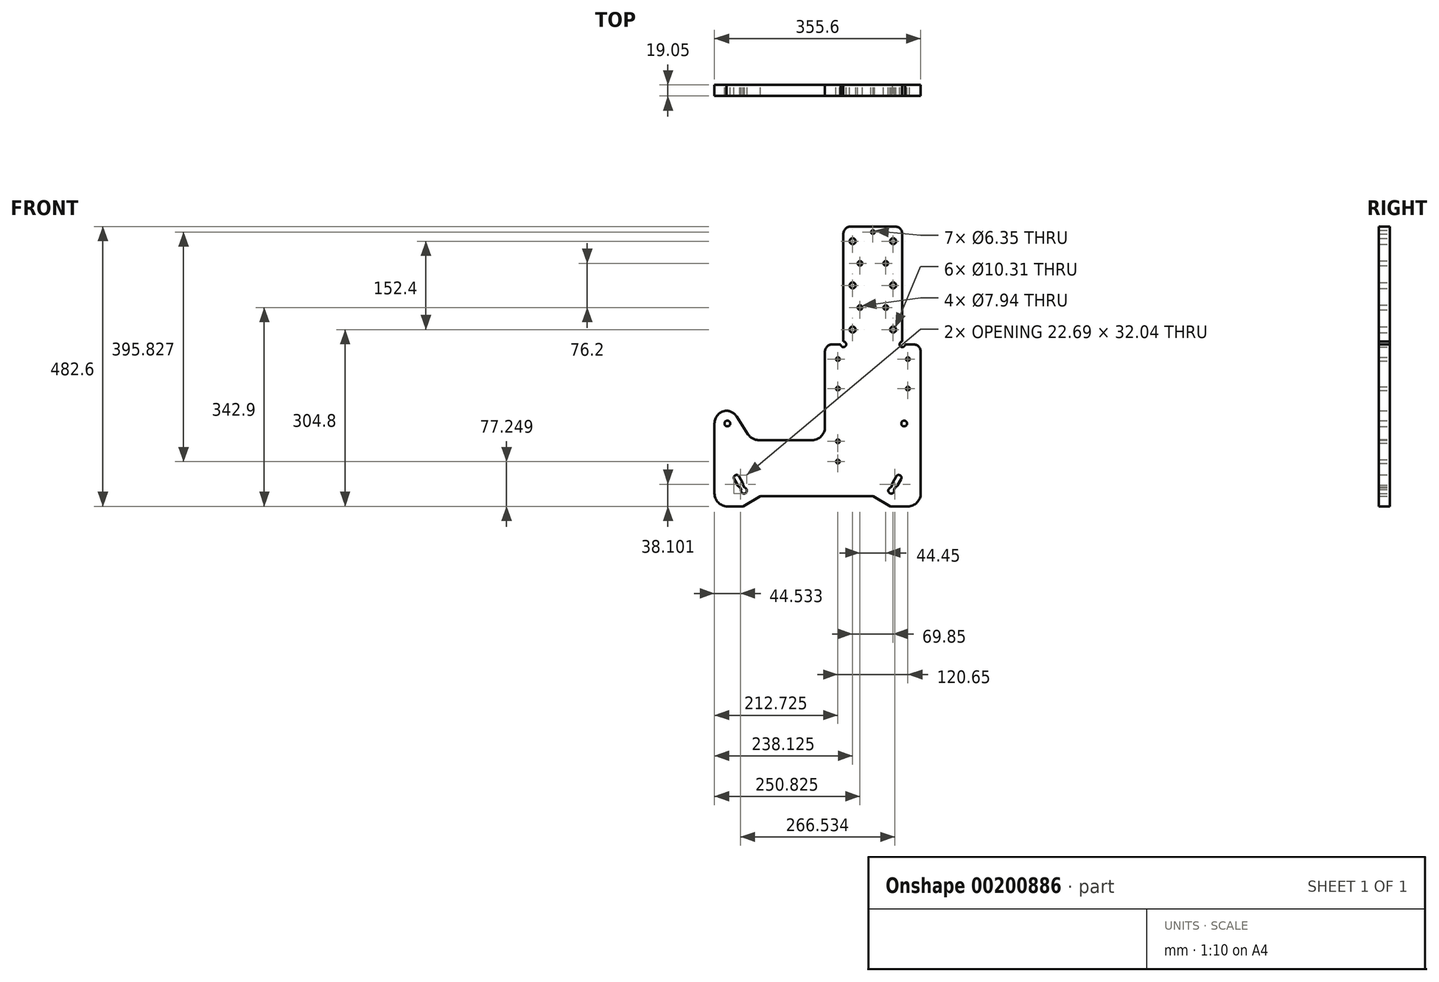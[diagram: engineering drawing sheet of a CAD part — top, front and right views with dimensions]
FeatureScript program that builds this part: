
annotation { "Feature Type Name" : "Feature", "Feature Type Description" : "" }
export const myFeature = defineFeature(function(context is Context, id is Id, definition is map)
    precondition{}
    {
        {
            var Q0;
            Q0=qCreatedBy(makeId("Front.planeOp"),FACE);
            var sketch = newSketch(context, id + "F0", { "sketchPlane" : qUnion([Q0])});
            skCircle(sketch, "E0", {"center": v(-155.58, -98.43) * mm, "radius": 4.95 * mm});
            skCircle(sketch, "E1", {"center": v(149.23, -98.43) * mm, "radius": 4.95 * mm});
            skCircle(sketch, "E2", {"center": v(60.33, 215.9) * mm, "radius": 5.16 * mm});
            skCircle(sketch, "E3", {"center": v(60.33, 139.7) * mm, "radius": 5.16 * mm});
            skCircle(sketch, "E4", {"center": v(60.33, 63.5) * mm, "radius": 5.16 * mm});
            skCircle(sketch, "E5", {"center": v(130.18, 63.5) * mm, "radius": 5.16 * mm});
            skCircle(sketch, "E6", {"center": v(130.18, 139.7) * mm, "radius": 5.16 * mm});
            skCircle(sketch, "E7", {"center": v(130.18, 215.9) * mm, "radius": 5.16 * mm});
            skCircle(sketch, "E8", {"center": v(95.25, 231.78) * mm, "radius": 3.18 * mm});
            skCircle(sketch, "E9", {"center": v(34.93, 12.7) * mm, "radius": 3.18 * mm});
            skCircle(sketch, "E10", {"center": v(34.93, -38.1) * mm, "radius": 3.18 * mm});
            skCircle(sketch, "E11", {"center": v(155.58, 12.7) * mm, "radius": 3.18 * mm});
            skCircle(sketch, "E12", {"center": v(155.58, -38.1) * mm, "radius": 3.18 * mm});
            skCircle(sketch, "E13", {"center": v(34.93, -129.13) * mm, "radius": 3.18 * mm});
            skCircle(sketch, "E14", {"center": v(34.93, -164.05) * mm, "radius": 3.18 * mm});
            skCircle(sketch, "E15", {"center": v(73.03, 177.8) * mm, "radius": 3.97 * mm});
            skCircle(sketch, "E16", {"center": v(117.48, 177.8) * mm, "radius": 3.97 * mm});
            skCircle(sketch, "E17", {"center": v(117.48, 101.6) * mm, "radius": 3.97 * mm});
            skCircle(sketch, "E18", {"center": v(73.03, 101.6) * mm, "radius": 3.97 * mm});
            skLineSegment(sketch, "E19", {"start": v(165.1, 38.1) * mm, "end": v(150.81, 38.1) * mm});
            skLineSegment(sketch, "E20", {"start": v(177.8, -219.08) * mm, "end": v(177.8, 25.4) * mm});
            skLineSegment(sketch, "E21", {"start": v(125.41, -241.3) * mm, "end": v(95.4, -223.97) * mm});
            skLineSegment(sketch, "E22", {"start": v(95.4, -223.97) * mm, "end": v(-98.57, -223.97) * mm});
            skLineSegment(sketch, "E23", {"start": v(-98.57, -223.97) * mm, "end": v(-128.59, -241.3) * mm});
            skLineSegment(sketch, "E24", {"start": v(-177.8, -98.43) * mm, "end": v(-177.8, -219.08) * mm});
            skLineSegment(sketch, "E25", {"start": v(-120.19, -116.73) * mm, "end": v(-139.5, -86.47) * mm});
            skLineSegment(sketch, "E26", {"start": v(-9.53, -127) * mm, "end": v(-101.45, -127) * mm});
            skLineSegment(sketch, "E27", {"start": v(12.7, 25.4) * mm, "end": v(12.7, -104.78) * mm});
            skLineSegment(sketch, "E28", {"start": v(39.69, 38.1) * mm, "end": v(25.4, 38.1) * mm});
            skLineSegment(sketch, "E29", {"start": v(44.45, 228.6) * mm, "end": v(44.45, 42.86) * mm});
            skLineSegment(sketch, "E30", {"start": v(133.35, 241.3) * mm, "end": v(57.15, 241.3) * mm});
            skLineSegment(sketch, "E31", {"start": v(146.05, 42.86) * mm, "end": v(146.05, 228.6) * mm});
            skLineSegment(sketch, "E32", {"start": v(-143.99, -194.56) * mm, "end": v(-137.64, -205.56) * mm});
            skLineSegment(sketch, "E33", {"start": v(-134.36, -207.93) * mm, "end": v(-131.84, -212.3) * mm});
            skLineSegment(sketch, "E34", {"start": v(-126.12, -209) * mm, "end": v(-128.64, -204.63) * mm});
            skLineSegment(sketch, "E35", {"start": v(-129.06, -200.6) * mm, "end": v(-135.41, -189.61) * mm});
            skLineSegment(sketch, "E36", {"start": v(135.41, -189.61) * mm, "end": v(129.06, -200.6) * mm});
            skLineSegment(sketch, "E37", {"start": v(128.64, -204.63) * mm, "end": v(126.12, -209) * mm});
            skLineSegment(sketch, "E38", {"start": v(131.84, -212.3) * mm, "end": v(134.36, -207.93) * mm});
            skLineSegment(sketch, "E39", {"start": v(137.64, -205.56) * mm, "end": v(143.99, -194.56) * mm});
            skLineSegment(sketch, "E40", {"start": v(-155.58, -241.3) * mm, "end": v(-128.59, -241.3) * mm});
            skLineSegment(sketch, "E41", {"start": v(125.41, -241.3) * mm, "end": v(155.58, -241.3) * mm});
            skLineSegment(sketch, "E42", {"start": v(-112.86, -232.22) * mm, "end": v(-122.22, -216.01) * mm, "construction": true});
            skLineSegment(sketch, "E43", {"start": v(-127.71, -219.2) * mm, "end": v(-118.36, -235.4) * mm, "construction": true});
            skLineSegment(sketch, "E44", {"start": v(117.5, -236.73) * mm, "end": v(127.61, -219.2) * mm, "construction": true});
            skLineSegment(sketch, "E45", {"start": v(122.18, -215.92) * mm, "end": v(112, -233.55) * mm, "construction": true});
            skLineSegment(sketch, "E46", {"start": v(146.05, 219.08) * mm, "end": v(134.25, 219.08) * mm, "construction": true});
            skLineSegment(sketch, "E47", {"start": v(134.26, 212.73) * mm, "end": v(146.05, 212.73) * mm, "construction": true});
            skLineSegment(sketch, "E48", {"start": v(146.05, 142.88) * mm, "end": v(134.25, 142.88) * mm, "construction": true});
            skLineSegment(sketch, "E49", {"start": v(134.26, 136.53) * mm, "end": v(146.05, 136.53) * mm, "construction": true});
            skLineSegment(sketch, "E50", {"start": v(146.05, 66.68) * mm, "end": v(134.25, 66.68) * mm, "construction": true});
            skLineSegment(sketch, "E51", {"start": v(134.26, 60.33) * mm, "end": v(146.05, 60.33) * mm, "construction": true});
            skLineSegment(sketch, "E52", {"start": v(44.45, 136.53) * mm, "end": v(56.24, 136.53) * mm, "construction": true});
            skLineSegment(sketch, "E53", {"start": v(56.25, 142.88) * mm, "end": v(44.45, 142.88) * mm, "construction": true});
            skLineSegment(sketch, "E54", {"start": v(44.45, 212.73) * mm, "end": v(56.24, 212.73) * mm, "construction": true});
            skLineSegment(sketch, "E55", {"start": v(56.25, 219.08) * mm, "end": v(44.45, 219.08) * mm, "construction": true});
            skLineSegment(sketch, "E56", {"start": v(44.45, 60.33) * mm, "end": v(56.24, 60.33) * mm, "construction": true});
            skLineSegment(sketch, "E57", {"start": v(56.25, 66.68) * mm, "end": v(44.45, 66.68) * mm, "construction": true});
            skArc(sketch, "E58", {"start": v(146.05, 42.86) * mm, "mid": v(142.68, 34.73) * mm, "end": v(150.81, 38.1) * mm});
            skArc(sketch, "E59", {"start": v(177.8, 25.4) * mm, "mid": v(174.08, 34.38) * mm, "end": v(165.1, 38.1) * mm});
            skArc(sketch, "E60", {"start": v(155.58, -241.3) * mm, "mid": v(171.3, -234.8) * mm, "end": v(177.8, -219.08) * mm});
            skArc(sketch, "E61", {"start": v(-177.8, -219.08) * mm, "mid": v(-171.3, -234.8) * mm, "end": v(-155.58, -241.3) * mm});
            skArc(sketch, "E62", {"start": v(-156.9, -76.24) * mm, "mid": v(-171.75, -83.19) * mm, "end": v(-177.8, -98.43) * mm});
            skArc(sketch, "E63", {"start": v(-139.5, -86.47) * mm, "mid": v(-146.97, -79.26) * mm, "end": v(-156.9, -76.24) * mm});
            skArc(sketch, "E64", {"start": v(-120.19, -116.73) * mm, "mid": v(-112.14, -124.26) * mm, "end": v(-101.45, -127) * mm});
            skArc(sketch, "E65", {"start": v(-9.53, -127) * mm, "mid": v(6.2, -120.5) * mm, "end": v(12.7, -104.78) * mm});
            skArc(sketch, "E66", {"start": v(25.4, 38.1) * mm, "mid": v(16.42, 34.38) * mm, "end": v(12.7, 25.4) * mm});
            skArc(sketch, "E67", {"start": v(39.69, 38.1) * mm, "mid": v(47.82, 34.73) * mm, "end": v(44.45, 42.86) * mm});
            skArc(sketch, "E68", {"start": v(57.15, 241.3) * mm, "mid": v(48.17, 237.58) * mm, "end": v(44.45, 228.6) * mm});
            skArc(sketch, "E69", {"start": v(146.05, 228.6) * mm, "mid": v(142.33, 237.58) * mm, "end": v(133.35, 241.3) * mm});
            skArc(sketch, "E70", {"start": v(-135.41, -189.61) * mm, "mid": v(-142.18, -187.8) * mm, "end": v(-143.99, -194.56) * mm});
            skArc(sketch, "E71", {"start": v(-137.64, -205.56) * mm, "mid": v(-136.25, -207.1) * mm, "end": v(-134.36, -207.93) * mm});
            skArc(sketch, "E72", {"start": v(-131.84, -212.3) * mm, "mid": v(-124.42, -218.55) * mm, "end": v(-126.12, -209) * mm});
            skArc(sketch, "E73", {"start": v(-128.64, -204.63) * mm, "mid": v(-128.42, -202.58) * mm, "end": v(-129.06, -200.6) * mm});
            skArc(sketch, "E74", {"start": v(143.99, -194.56) * mm, "mid": v(142.18, -187.8) * mm, "end": v(135.41, -189.61) * mm});
            skArc(sketch, "E75", {"start": v(129.06, -200.6) * mm, "mid": v(128.42, -202.58) * mm, "end": v(128.64, -204.63) * mm});
            skArc(sketch, "E76", {"start": v(126.12, -209) * mm, "mid": v(124.42, -218.55) * mm, "end": v(131.84, -212.3) * mm});
            skArc(sketch, "E77", {"start": v(134.36, -207.93) * mm, "mid": v(136.25, -207.1) * mm, "end": v(137.64, -205.56) * mm});
            skSolve(sketch);
        }
        {
            var Q0;
            Q0 = qSketchRegion(id + "F0", true);
            extrude(context, id + "F1", {"entities" : qUnion([Q0]), "depth" : 19.05 * mm});
        }
    });
